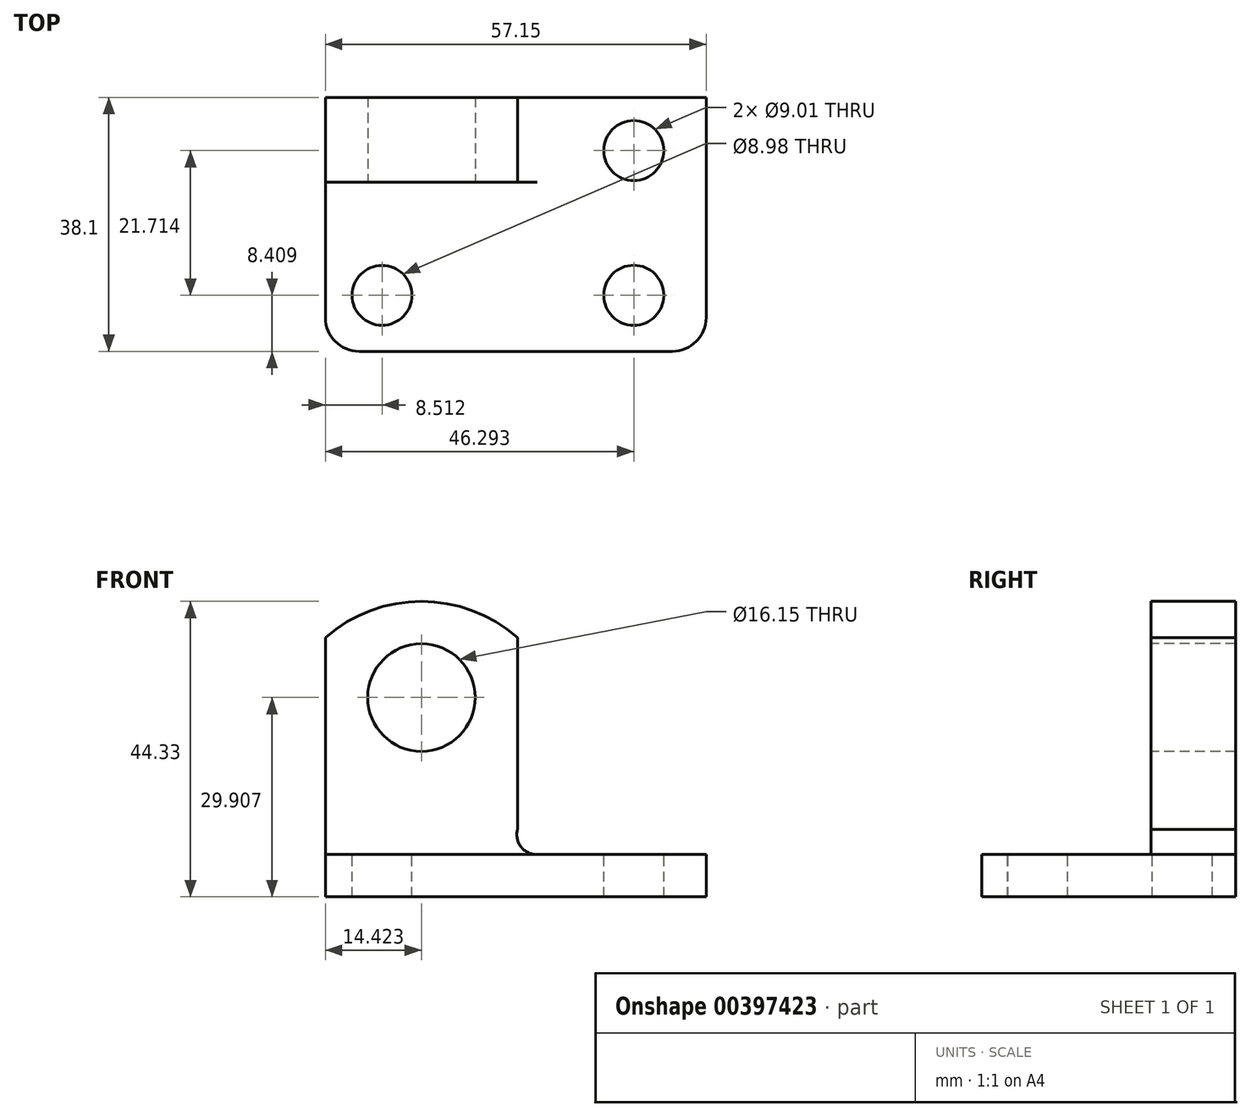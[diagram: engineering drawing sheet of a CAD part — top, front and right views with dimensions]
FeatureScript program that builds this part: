
annotation { "Feature Type Name" : "Feature", "Feature Type Description" : "" }
export const myFeature = defineFeature(function(context is Context, id is Id, definition is map)
    precondition{}
    {
        {
            var Q0;
            Q0=qCreatedBy(makeId("Front.planeOp"),FACE);
            var sketch = newSketch(context, id + "F0", { "sketchPlane" : qUnion([Q0])});
            skLineSegment(sketch, "E0", {"start": v(0, 6.35) * mm, "end": v(0, 0) * mm});
            skLineSegment(sketch, "E1", {"start": v(0, 0) * mm, "end": v(57.15, 0) * mm});
            skLineSegment(sketch, "E2", {"start": v(57.15, 0) * mm, "end": v(57.15, 6.35) * mm});
            skLineSegment(sketch, "E3", {"start": v(57.15, 6.35) * mm, "end": v(0, 6.35) * mm});
            skSolve(sketch);
        }
        {
            var Q0;
            Q0 = qSketchRegion(id + "F0", true);
            extrude(context, id + "F1", {"entities" : qUnion([Q0]), "depth" : 38.1 * mm});
        }
        {
            var Q0;
            Q0=makeQuery(id+"F1.opExtrude","CAP_EDGE",EDGE,{"disambiguationData":[OSD([sQuery(id+"F0.wireOp",EDGE,"E0")])],"isStart":false});
            var Q1;
            Q1=makeQuery(id+"F1.opExtrude","CAP_EDGE",EDGE,{"disambiguationData":[OSD([sQuery(id+"F0.wireOp",EDGE,"E2")])],"isStart":false});
            fillet(context, id + "F2", {"entities" : qUnion([Q0, Q1]), "radius" : 5.08 * mm, "tangentPropagation" : true, "allowEdgeOverflow" : false});
        }
        {
            var Q0;
            Q0=qCreatedBy(makeId("Front.planeOp"),FACE);
            var sketch = newSketch(context, id + "F3", { "sketchPlane" : qUnion([Q0])});
            skLineSegment(sketch, "E4", {"start": v(0, 6.25) * mm, "end": v(0, 44.35) * mm});
            skLineSegment(sketch, "E5", {"start": v(0, 44.35) * mm, "end": v(31.75, 44.35) * mm});
            skLineSegment(sketch, "E6", {"start": v(31.75, 44.35) * mm, "end": v(31.75, 6.25) * mm});
            skLineSegment(sketch, "E7", {"start": v(31.75, 6.25) * mm, "end": v(0, 6.25) * mm});
            skSolve(sketch);
        }
        {
            var Q0;
            Q0=makeQuery(id+"F3.imprint","IMPRINT",FACE,{"disambiguationData":[TD([[makeQuery(id+"F3.imprint","IMPRINT",EDGE,{"derivedFrom":sQuery(id+"F3.wireOp",EDGE,"E4")}),-1.0]])]});
            extrude(context, id + "F4", {"entities" : qUnion([Q0]), "operationType" : NewBodyOperationType.ADD, "depth" : 12.7 * mm});
        }
        {
            var Q0;
            Q0=makeQuery(id+"F4.opExtrude","CAP_FACE",FACE,{"disambiguationData":[OSD([sQuery(id+"F3.wireOp",EDGE,"E4"),sQuery(id+"F3.wireOp",EDGE,"E5"),sQuery(id+"F3.wireOp",EDGE,"E6"),sQuery(id+"F3.wireOp",EDGE,"E7")])],"isStart":false});
            var sketch = newSketch(context, id + "F5", { "sketchPlane" : qUnion([Q0])});
            skArc(sketch, "E8", {"start": v(28.85, 10.15) * mm, "mid": v(29.36, 7.53) * mm, "end": v(31.75, 6.35) * mm});
            skLineSegment(sketch, "E9", {"start": v(28.85, 10.15) * mm, "end": v(28.85, 38.9) * mm});
            skArc(sketch, "E10", {"start": v(28.85, 38.9) * mm, "mid": v(14.42, 44.33) * mm, "end": v(0, 38.9) * mm});
            skSolve(sketch);
        }
        {
            var Q0;
            Q0=makeQuery(id+"F5.imprint","IMPRINT",FACE,{"disambiguationData":[TD([[makeQuery(id+"F5.imprint","IMPRINT",EDGE,{"derivedFrom":sQuery(id+"F5.wireOp",EDGE,"E8")}),1.0]])]});
            extrude(context, id + "F6", {"entities" : qUnion([Q0]), "operationType" : NewBodyOperationType.REMOVE, "oppositeDirection" : true, "depth" : 25.4 * mm});
        }
        {
            var Q0;
            Q0=makeQuery(id+"F4.opExtrude","CAP_FACE",FACE,{"disambiguationData":[OSD([sQuery(id+"F3.wireOp",EDGE,"E4"),sQuery(id+"F3.wireOp",EDGE,"E5"),sQuery(id+"F3.wireOp",EDGE,"E6"),sQuery(id+"F3.wireOp",EDGE,"E7")])],"isStart":false});
            var sketch = newSketch(context, id + "F7", { "sketchPlane" : qUnion([Q0])});
            skCircle(sketch, "E11", {"center": v(14.42, 29.9) * mm, "radius": 8.07 * mm});
            skSolve(sketch);
        }
        {
            var Q0;
            Q0=makeQuery(id+"F7.imprint","IMPRINT",FACE,{"disambiguationData":[TD([[makeQuery(id+"F7.imprint","IMPRINT",EDGE,{"derivedFrom":sQuery(id+"F7.wireOp",EDGE,"E11")}),1.0]])]});
            extrude(context, id + "F8", {"entities" : qUnion([Q0]), "operationType" : NewBodyOperationType.REMOVE, "oppositeDirection" : true, "depth" : 25.4 * mm});
        }
        {
            var Q0;
            Q0=makeQuery(id+"F1.opExtrude","SWEPT_FACE",FACE,{"disambiguationData":[OSD([sQuery(id+"F0.wireOp",EDGE,"E3")])]});
            var sketch = newSketch(context, id + "F9", { "sketchPlane" : qUnion([Q0])});
            skCircle(sketch, "E12", {"center": v(46.3, -29.7) * mm, "radius": 4.5 * mm});
            skCircle(sketch, "E13", {"center": v(46.3, -7.98) * mm, "radius": 4.5 * mm});
            skCircle(sketch, "E14", {"center": v(8.51, -29.7) * mm, "radius": 4.49 * mm});
            skSolve(sketch);
        }
        {
            var Q0;
            Q0 = qSketchRegion(id + "F9", true);
            extrude(context, id + "F10", {"entities" : qUnion([Q0]), "operationType" : NewBodyOperationType.REMOVE, "oppositeDirection" : true, "depth" : 25.4 * mm});
        }
    });
